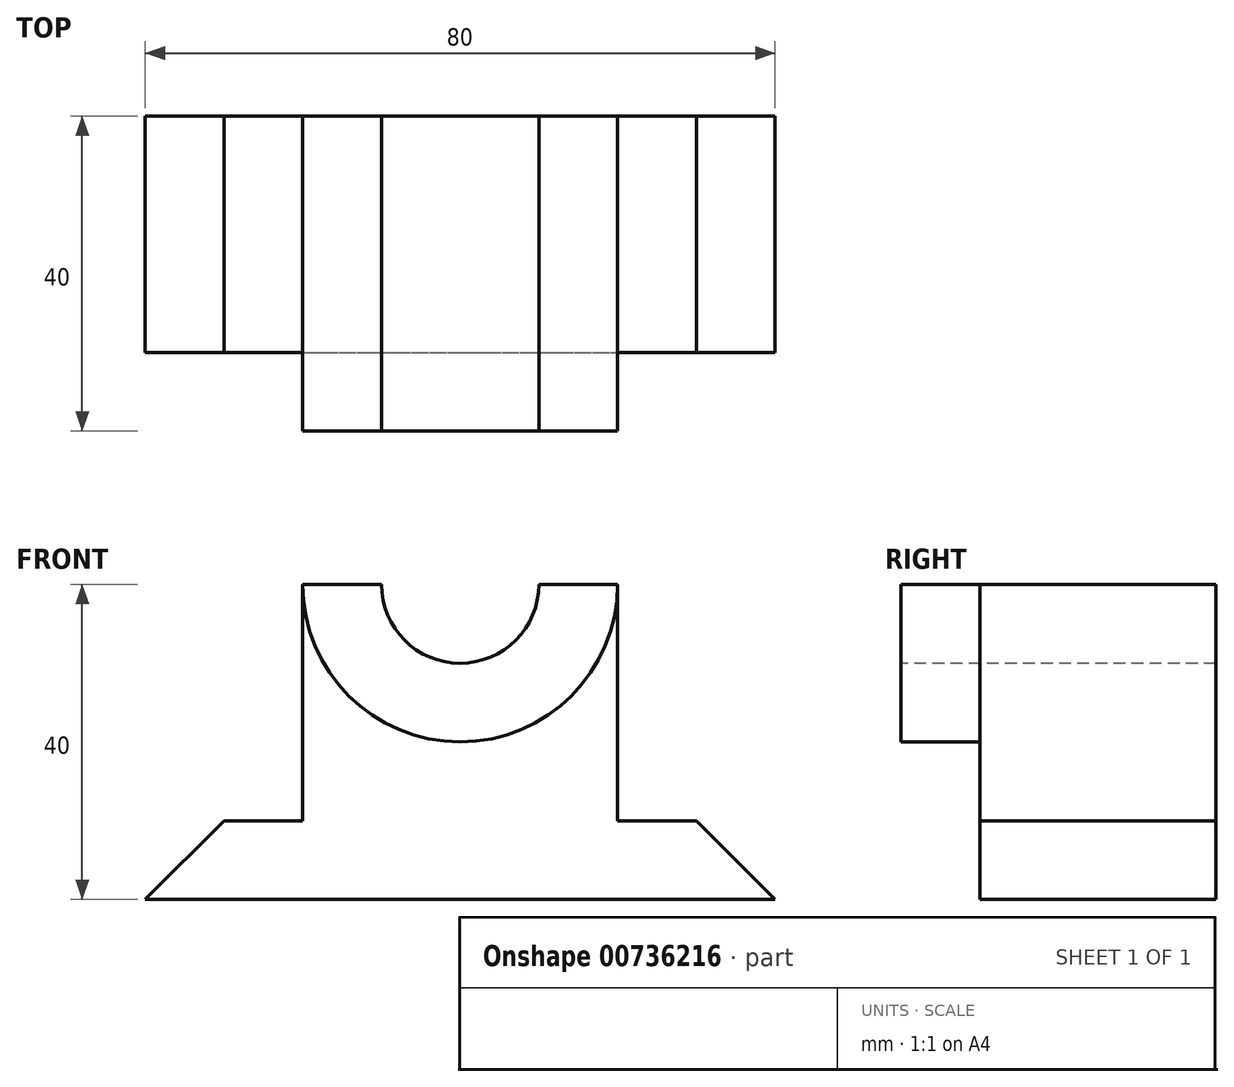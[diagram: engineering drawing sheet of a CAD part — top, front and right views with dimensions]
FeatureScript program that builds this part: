
annotation { "Feature Type Name" : "Feature", "Feature Type Description" : "" }
export const myFeature = defineFeature(function(context is Context, id is Id, definition is map)
    precondition{}
    {
        {
            var Q0;
            Q0=qCreatedBy(makeId("Front.planeOp"),FACE);
            var sketch = newSketch(context, id + "F0", { "sketchPlane" : qUnion([Q0])});
            skLineSegment(sketch, "E0", {"start": v(0, 0) * mm, "end": v(80, 0) * mm});
            skLineSegment(sketch, "E1", {"start": v(80, 0) * mm, "end": v(70, 10) * mm});
            skLineSegment(sketch, "E2", {"start": v(70, 10) * mm, "end": v(60, 10) * mm});
            skLineSegment(sketch, "E3", {"start": v(60, 10) * mm, "end": v(60, 40) * mm});
            skLineSegment(sketch, "E4", {"start": v(60, 40) * mm, "end": v(20, 40) * mm});
            skLineSegment(sketch, "E5", {"start": v(20, 40) * mm, "end": v(20, 10) * mm});
            skLineSegment(sketch, "E6", {"start": v(20, 10) * mm, "end": v(10, 10) * mm});
            skLineSegment(sketch, "E7", {"start": v(10, 10) * mm, "end": v(0, 0) * mm});
            skSolve(sketch);
        }
        {
            var Q0;
            Q0=makeQuery(id+"F0.imprint","IMPRINT",FACE,{"disambiguationData":[TD([[makeQuery(id+"F0.imprint","IMPRINT",EDGE,{"derivedFrom":sQuery(id+"F0.wireOp",EDGE,"E0")}),1.0]])]});
            extrude(context, id + "F1", {"entities" : qUnion([Q0]), "depth" : 30 * mm, "offsetDistance" : 25 * mm});
        }
        {
            var Q0;
            Q0=makeQuery(id+"F1.opExtrude","CAP_FACE",FACE,{"disambiguationData":[OSD([sQuery(id+"F0.wireOp",EDGE,"E0"),sQuery(id+"F0.wireOp",EDGE,"E1"),sQuery(id+"F0.wireOp",EDGE,"E2"),sQuery(id+"F0.wireOp",EDGE,"E3"),sQuery(id+"F0.wireOp",EDGE,"E4"),sQuery(id+"F0.wireOp",EDGE,"E5"),sQuery(id+"F0.wireOp",EDGE,"E6"),sQuery(id+"F0.wireOp",EDGE,"E7")])],"isStart":false});
            var sketch = newSketch(context, id + "F2", { "sketchPlane" : qUnion([Q0])});
            skArc(sketch, "E8", {"start": v(20, 40) * mm, "mid": v(40, 20) * mm, "end": v(60, 40) * mm});
            skLineSegment(sketch, "E9", {"start": v(20, 40) * mm, "end": v(60, 40) * mm});
            skSolve(sketch);
        }
        {
            var Q0;
            Q0=makeQuery(id+"F2.imprint","IMPRINT",FACE,{"disambiguationData":[TD([[makeQuery(id+"F2.imprint","IMPRINT",EDGE,{"derivedFrom":sQuery(id+"F2.wireOp",EDGE,"E8")}),1.0]])]});
            extrude(context, id + "F3", {"entities" : qUnion([Q0]), "operationType" : NewBodyOperationType.ADD, "depth" : 10 * mm, "offsetDistance" : 25 * mm});
        }
        {
            var Q0;
            Q0=makeQuery(id+"F3.opExtrude","CAP_FACE",FACE,{"disambiguationData":[OSD([sQuery(id+"F2.wireOp",EDGE,"E8"),sQuery(id+"F2.wireOp",EDGE,"E9")])],"isStart":false});
            var sketch = newSketch(context, id + "F4", { "sketchPlane" : qUnion([Q0])});
            skArc(sketch, "E10", {"start": v(50, 40) * mm, "mid": v(40, 30) * mm, "end": v(30, 40) * mm});
            skLineSegment(sketch, "E11", {"start": v(30, 40) * mm, "end": v(50, 40) * mm});
            skSolve(sketch);
        }
        {
            var Q0;
            Q0 = qSketchRegion(id + "F4", true);
            extrude(context, id + "F5", {"entities" : qUnion([Q0]), "operationType" : NewBodyOperationType.REMOVE, "oppositeDirection" : true, "depth" : 43.3 * mm, "offsetDistance" : 25 * mm});
        }
    });
